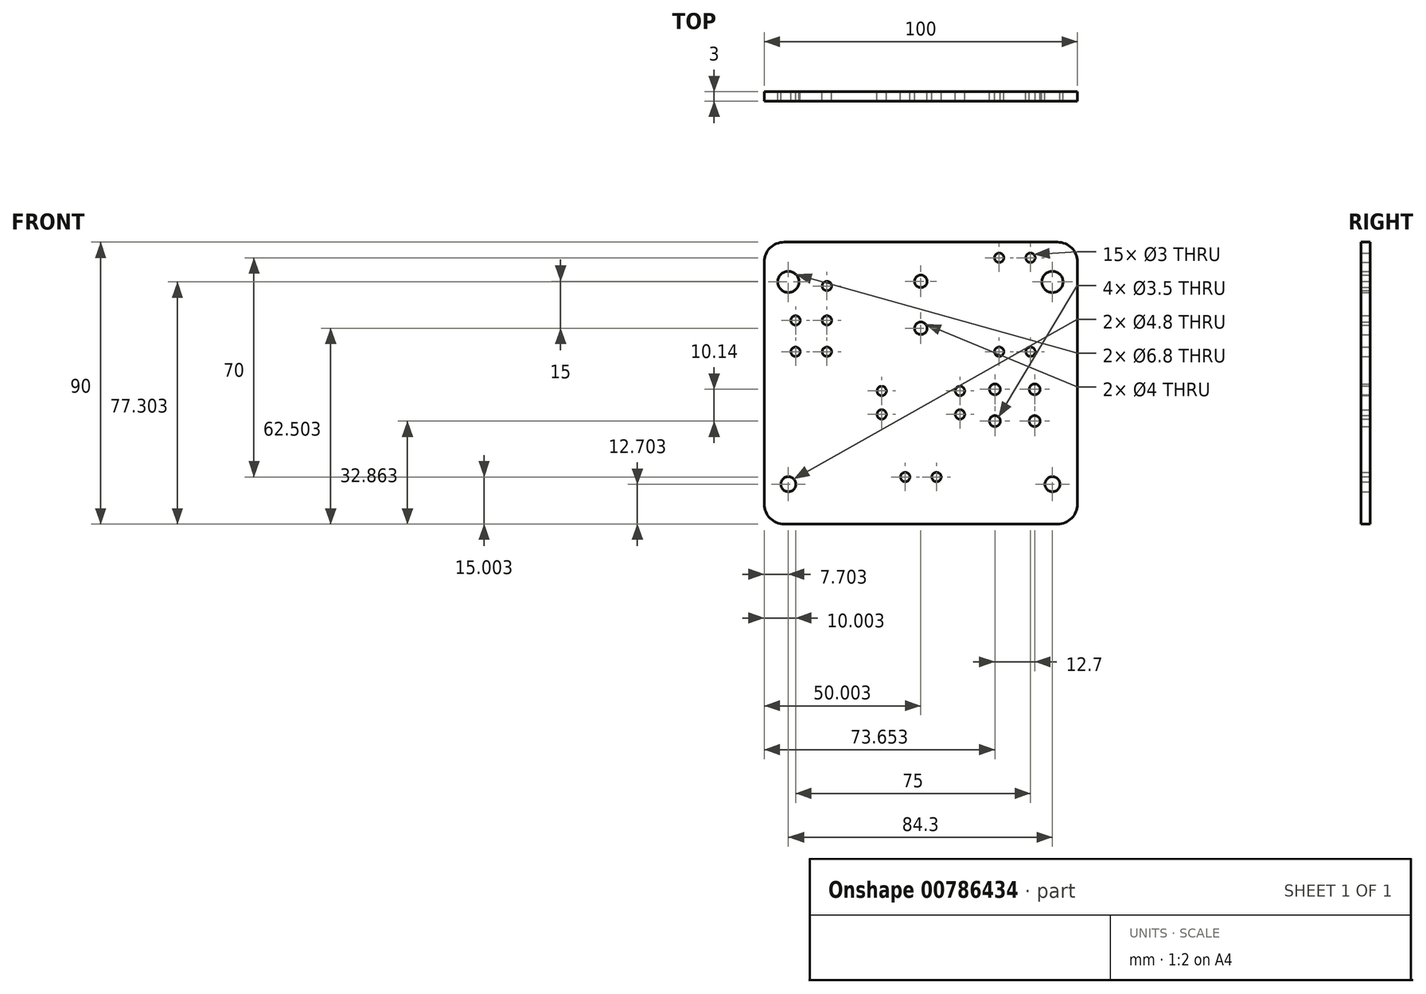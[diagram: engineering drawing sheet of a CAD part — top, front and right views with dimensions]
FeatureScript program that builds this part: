
annotation { "Feature Type Name" : "Feature", "Feature Type Description" : "" }
export const myFeature = defineFeature(function(context is Context, id is Id, definition is map)
    precondition{}
    {
        {
            var Q0;
            Q0=qCreatedBy(makeId("Front.planeOp"),FACE);
            var sketch = newSketch(context, id + "F0", { "sketchPlane" : qUnion([Q0])});
            skArc(sketch, "E0", {"start": v(45.97, 34.48) * mm, "mid": v(44.11, 38.97) * mm, "end": v(39.62, 40.83) * mm});
            skLineSegment(sketch, "E1", {"start": v(45.97, -42.82) * mm, "end": v(45.97, 34.48) * mm});
            skArc(sketch, "E2", {"start": v(39.62, -49.17) * mm, "mid": v(44.11, -47.3) * mm, "end": v(45.97, -42.82) * mm});
            skArc(sketch, "E3", {"start": v(-47.68, 40.83) * mm, "mid": v(-52.17, 38.97) * mm, "end": v(-54.03, 34.48) * mm});
            skLineSegment(sketch, "E4", {"start": v(-54.03, -42.82) * mm, "end": v(-54.03, 34.48) * mm});
            skArc(sketch, "E5", {"start": v(-54.03, -42.82) * mm, "mid": v(-52.17, -47.3) * mm, "end": v(-47.68, -49.17) * mm});
            skLineSegment(sketch, "E6", {"start": v(-47.68, 40.83) * mm, "end": v(39.62, 40.83) * mm});
            skLineSegment(sketch, "E7", {"start": v(39.62, -49.17) * mm, "end": v(-47.68, -49.17) * mm});
            skCircle(sketch, "E8", {"center": v(-4.03, 13.33) * mm, "radius": 2 * mm});
            skCircle(sketch, "E9", {"center": v(-4.03, 28.33) * mm, "radius": 2 * mm});
            skCircle(sketch, "E10", {"center": v(19.62, -6.17) * mm, "radius": 1.75 * mm});
            skCircle(sketch, "E11", {"center": v(19.62, -16.3) * mm, "radius": 1.75 * mm});
            skCircle(sketch, "E12", {"center": v(32.32, -6.17) * mm, "radius": 1.75 * mm});
            skCircle(sketch, "E13", {"center": v(32.32, -16.3) * mm, "radius": 1.75 * mm});
            skCircle(sketch, "E14", {"center": v(-16.53, -14.17) * mm, "radius": 1.5 * mm});
            skCircle(sketch, "E15", {"center": v(8.47, -14.17) * mm, "radius": 1.5 * mm});
            skCircle(sketch, "E16", {"center": v(-16.53, -6.67) * mm, "radius": 1.5 * mm});
            skCircle(sketch, "E17", {"center": v(8.47, -6.67) * mm, "radius": 1.5 * mm});
            skCircle(sketch, "E18", {"center": v(0.97, -34.17) * mm, "radius": 1.5 * mm});
            skCircle(sketch, "E19", {"center": v(-9.03, -34.17) * mm, "radius": 1.5 * mm});
            skCircle(sketch, "E20", {"center": v(-46.33, 28.13) * mm, "radius": 3.4 * mm});
            skCircle(sketch, "E21", {"center": v(37.97, 28.13) * mm, "radius": 3.4 * mm});
            skCircle(sketch, "E22", {"center": v(-46.33, -36.47) * mm, "radius": 2.4 * mm});
            skCircle(sketch, "E23", {"center": v(37.97, -36.47) * mm, "radius": 2.4 * mm});
            skCircle(sketch, "E24", {"center": v(20.97, 35.83) * mm, "radius": 1.5 * mm});
            skCircle(sketch, "E25", {"center": v(30.97, 35.83) * mm, "radius": 1.5 * mm});
            skCircle(sketch, "E26", {"center": v(20.97, 5.83) * mm, "radius": 1.5 * mm});
            skCircle(sketch, "E27", {"center": v(30.97, 5.83) * mm, "radius": 1.5 * mm});
            skCircle(sketch, "E28", {"center": v(-44.03, 15.83) * mm, "radius": 1.5 * mm});
            skCircle(sketch, "E29", {"center": v(-34.03, 15.83) * mm, "radius": 1.5 * mm});
            skCircle(sketch, "E30", {"center": v(-34.03, 26.83) * mm, "radius": 1.5 * mm});
            skCircle(sketch, "E31", {"center": v(-44.03, 5.83) * mm, "radius": 1.5 * mm});
            skCircle(sketch, "E32", {"center": v(-34.03, 5.83) * mm, "radius": 1.5 * mm});
            skSolve(sketch);
        }
        {
            var Q0;
            Q0 = qSketchRegion(id + "F0", true);
            extrude(context, id + "F1", {"entities" : qUnion([Q0]), "depth" : 3 * mm, "offsetDistance" : 25 * mm});
        }
    });
